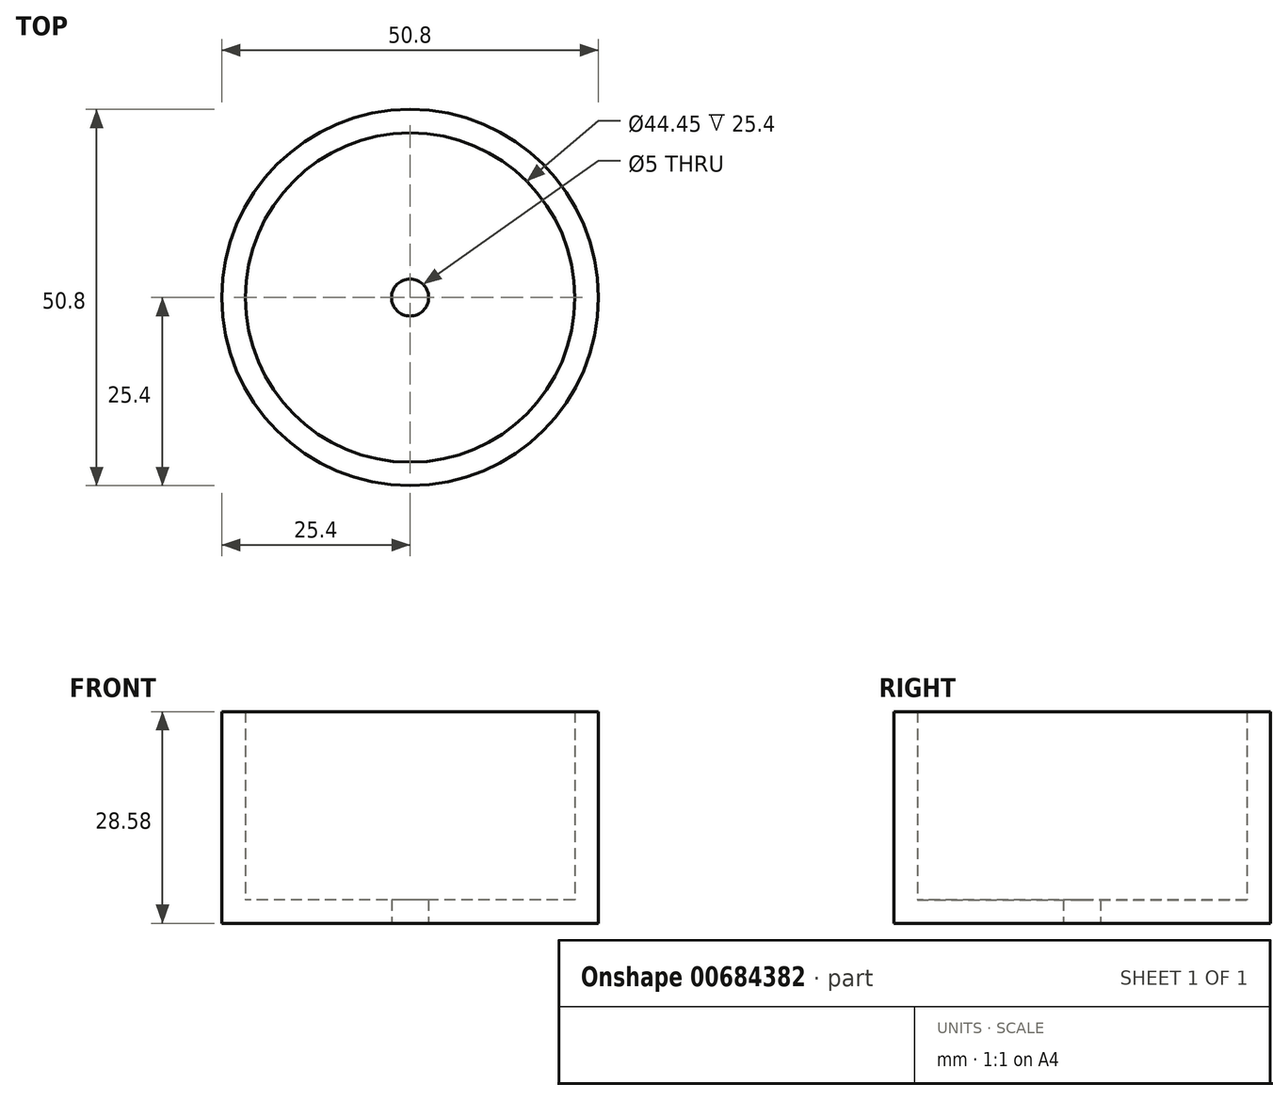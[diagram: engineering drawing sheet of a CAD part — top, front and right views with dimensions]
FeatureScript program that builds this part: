
annotation { "Feature Type Name" : "Feature", "Feature Type Description" : "" }
export const myFeature = defineFeature(function(context is Context, id is Id, definition is map)
    precondition{}
    {
        {
            var Q0;
            Q0=qCreatedBy(makeId("Top.planeOp"),FACE);
            var sketch = newSketch(context, id + "F0", { "sketchPlane" : qUnion([Q0])});
            skCircle(sketch, "E0", {"center": v(0, 0) * mm, "radius": 25.4 * mm});
            skSolve(sketch);
        }
        {
            var Q0;
            Q0=makeQuery(id+"F0.imprint","IMPRINT",FACE,{"disambiguationData":[TD([[makeQuery(id+"F0.imprint","IMPRINT",EDGE,{"derivedFrom":sQuery(id+"F0.wireOp",EDGE,"E0")}),1.0]])]});
            extrude(context, id + "F1", {"entities" : qUnion([Q0]), "depth" : 3.17 * mm, "offsetDistance" : 25.4 * mm});
        }
        {
            var Q0;
            Q0=makeQuery(id+"F1.opExtrude","CAP_FACE",FACE,{"disambiguationData":[OSD([sQuery(id+"F0.wireOp",EDGE,"E0")])],"isStart":false});
            var sketch = newSketch(context, id + "F2", { "sketchPlane" : qUnion([Q0])});
            skCircle(sketch, "E1.0", {"center": v(0, 0) * mm, "radius": 22.23 * mm});
            skSolve(sketch);
        }
        {
            var Q0;
            Q0=makeQuery(id+"F2.imprint","IMPRINT",FACE,{"disambiguationData":[TD([[makeQuery(id+"F2.imprint","IMPRINT",EDGE,{"derivedFrom":sQuery(id+"F2.wireOp",EDGE,"E1.0")}),-1.0]])]});
            extrude(context, id + "F3", {"entities" : qUnion([Q0]), "operationType" : NewBodyOperationType.ADD, "depth" : 25.4 * mm, "offsetDistance" : 25.4 * mm});
        }
        {
            var Q0;
            Q0=sQuery(id+"F0.wireOp",VERTEX,"E0.center");
            var Q1;
            Q1=makeQuery(id+"F1.opExtrude","SWEPT_BODY",BODY,{"disambiguationData":[OSD([sQuery(id+"F0.wireOp",EDGE,"E0")])]});
            hole(context, id + "F4", {"style" : HoleStyle.SIMPLE, "endStyle" : HoleEndStyle.THROUGH, "oppositeDirection" : true, "holeDiameter" : 5 * mm, "majorDiameter" : 6.35 * mm, "isTappedThrough" : true, "tappedDepth" : 12.7 * mm, "tapClearance" : 3, "startFromSketch" : true, "locations" : qUnion([Q0]), "scope" : qUnion([Q1])});
        }
    });
